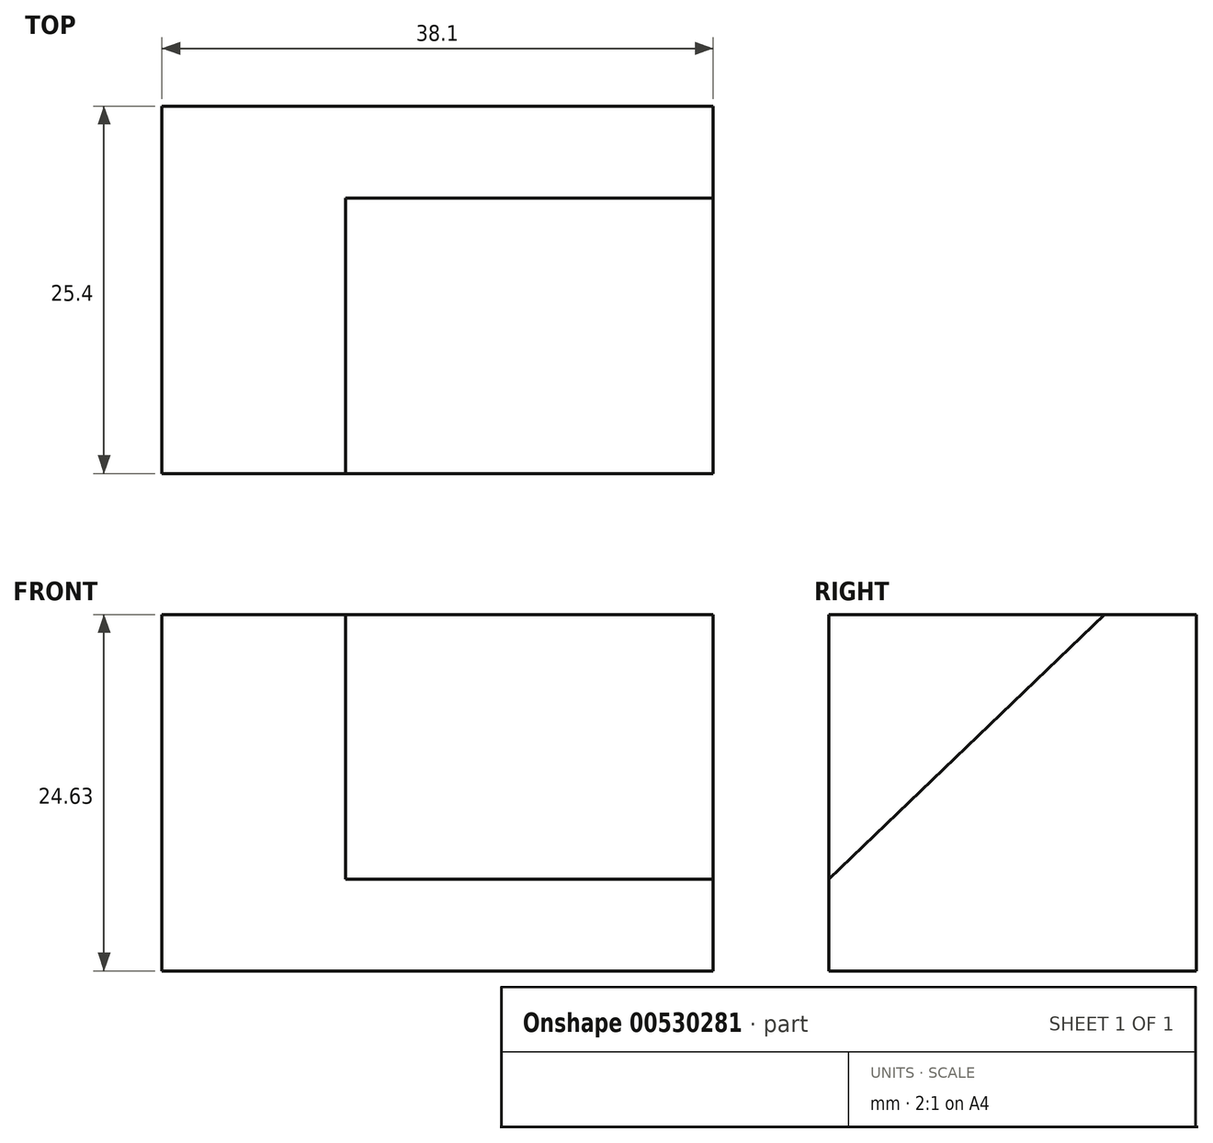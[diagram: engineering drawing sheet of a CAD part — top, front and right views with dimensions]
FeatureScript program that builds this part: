
annotation { "Feature Type Name" : "Feature", "Feature Type Description" : "" }
export const myFeature = defineFeature(function(context is Context, id is Id, definition is map)
    precondition{}
    {
        {
            var Q0;
            Q0=qCreatedBy(makeId("Front.planeOp"),FACE);
            var sketch = newSketch(context, id + "F0", { "sketchPlane" : qUnion([Q0])});
            skLineSegment(sketch, "E0.bottom", {"start": v(-49.46, 39.13) * mm, "end": v(-11.36, 39.13) * mm});
            skLineSegment(sketch, "E0.top", {"start": v(-49.46, 14.5) * mm, "end": v(-11.36, 14.5) * mm});
            skLineSegment(sketch, "E0.left", {"start": v(-49.46, 39.13) * mm, "end": v(-49.46, 14.5) * mm});
            skLineSegment(sketch, "E0.right", {"start": v(-11.36, 39.13) * mm, "end": v(-11.36, 14.5) * mm});
            skSolve(sketch);
        }
        {
            var Q0;
            Q0=makeQuery(id+"F0.imprint","IMPRINT",FACE,{"disambiguationData":[TD([[makeQuery(id+"F0.imprint","IMPRINT",EDGE,{"derivedFrom":sQuery(id+"F0.wireOp",EDGE,"E0.bottom")}),-1.0]])]});
            extrude(context, id + "F1", {"entities" : qUnion([Q0]), "depth" : 25.4 * mm, "offsetDistance" : 25.4 * mm});
        }
        {
            var Q0;
            Q0=makeQuery(id+"F1.opExtrude","SWEPT_FACE",FACE,{"disambiguationData":[OSD([sQuery(id+"F0.wireOp",EDGE,"E0.right")])]});
            var sketch = newSketch(context, id + "F2", { "sketchPlane" : qUnion([Q0])});
            skLineSegment(sketch, "E1", {"start": v(-6.35, 39.13) * mm, "end": v(-25.4, 20.85) * mm});
            skSolve(sketch);
        }
        {
            var Q0;
            {var subQ0=sQuery(id+"F2.wireOp",EDGE,"E1");Q0=makeQuery(id+"F2.imprint","IMPRINT",FACE,{"disambiguationData":[TD([[makeQuery(id+"F2.imprint","IMPRINT",EDGE,{"derivedFrom":subQ0}),-1.0]])]});}
            extrude(context, id + "F3", {"entities" : qUnion([Q0]), "operationType" : NewBodyOperationType.REMOVE, "oppositeDirection" : true, "depth" : 25.4 * mm, "offsetDistance" : 25.4 * mm});
        }
    });
